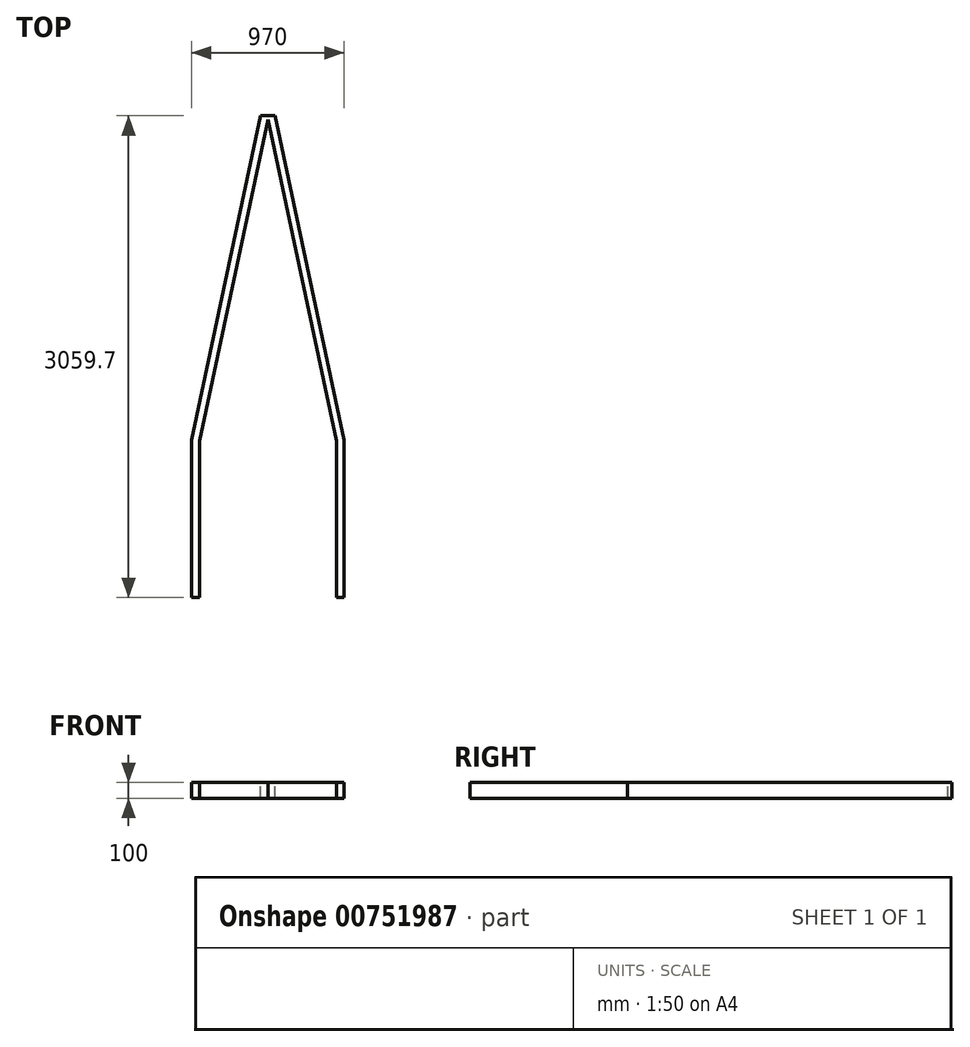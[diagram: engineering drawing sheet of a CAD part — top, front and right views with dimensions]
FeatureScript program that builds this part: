
annotation { "Feature Type Name" : "Feature", "Feature Type Description" : "" }
export const myFeature = defineFeature(function(context is Context, id is Id, definition is map)
    precondition{}
    {
        {
            var Q0;
            Q0=qCreatedBy(makeId("Top.planeOp"),FACE);
            var sketch = newSketch(context, id + "F0", { "sketchPlane" : qUnion([Q0])});
            skLineSegment(sketch, "E0", {"start": v(-485, -1000) * mm, "end": v(-485, 0) * mm});
            skLineSegment(sketch, "E1", {"start": v(-485, 0) * mm, "end": v(-45.6, 2059.7) * mm});
            skLineSegment(sketch, "E2", {"start": v(-325, 750) * mm, "end": v(0, 750) * mm, "construction": true});
            skLineSegment(sketch, "E3.0", {"start": v(-435, -5.27) * mm, "end": v(0, 2033.79) * mm});
            skLineSegment(sketch, "E3.1", {"start": v(-435, -1000) * mm, "end": v(-435, -5.27) * mm});
            skLineSegment(sketch, "E4", {"start": v(-485, -1000) * mm, "end": v(-435, -1000) * mm});
            skLineSegment(sketch, "E5.MirrorCS", {"start": v(485, -1000) * mm, "end": v(435, -1000) * mm});
            skLineSegment(sketch, "E6.MirrorCS", {"start": v(485, -1000) * mm, "end": v(485, 0) * mm});
            skLineSegment(sketch, "E7.MirrorCS", {"start": v(435, -1000) * mm, "end": v(435, -5.27) * mm});
            skLineSegment(sketch, "E8.MirrorCS", {"start": v(485, 0) * mm, "end": v(45.6, 2059.7) * mm});
            skLineSegment(sketch, "E9.MirrorCS", {"start": v(435, -5.27) * mm, "end": v(0, 2033.79) * mm});
            skLineSegment(sketch, "E10", {"start": v(-45.6, 2059.7) * mm, "end": v(45.6, 2059.7) * mm});
            skPoint(sketch, "E11.orphan", {"position": v(20.1, 1939.57) * mm});
            skPoint(sketch, "E12.orphan", {"position": v(69, 1950) * mm});
            skPoint(sketch, "E13.end.orphan", {"position": v(-20.1, 1939.57) * mm});
            skPoint(sketch, "E13.start.orphan", {"position": v(-69, 1950) * mm});
            skSolve(sketch);
        }
        {
            var Q0;
            Q0 = qSketchRegion(id + "F0", true);
            extrude(context, id + "F1", {"entities" : qUnion([Q0]), "oppositeDirection" : true, "depth" : 100 * mm, "offsetDistance" : 25 * mm});
        }
    });
